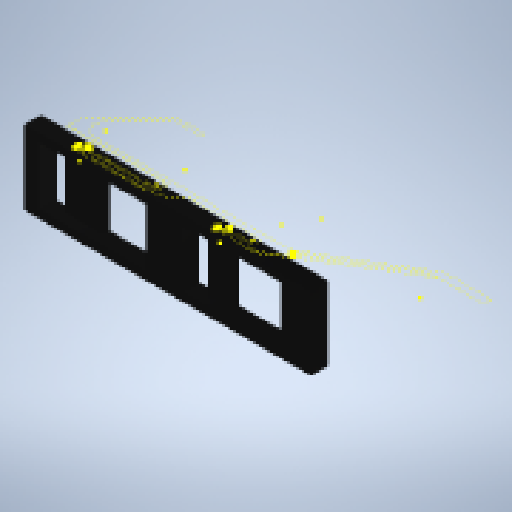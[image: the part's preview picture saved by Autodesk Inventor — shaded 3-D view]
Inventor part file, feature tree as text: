
AUTODESK INVENTOR PART (.ipt)
format: ipt  version: 2024.1 (Build 281209000, 209)  size: 655,360 bytes
history: native  units: mm
features: reference x29, projected_geometry x9, sketch x8, extrude x7, other x4, chamfer x4, plane x2, fillet x1
ambient origin geometry x8: Origin, YZ Plane, XZ Plane, XY Plane, X Axis, Y Axis, Z Axis, Center Point
bodies: Solid2 (feature_tree)
feature tree (64):
  other  "back-plate"
  plane  "Work Plane1"
  extrude  "Extrusion12"  Depth=19.0mm
  extrude  "Extrusion13"  Depth=47.0mm
  extrude  "Extrusion14"  Depth=19.2mm
  sketch  "Sketch14"  dims[d81=43.0mm]
  plane  "Work Plane2"
  chamfer  "Chamfer10"  Distance=1.5mm
  extrude  "Extrusion15"  Depth=15.0mm
  chamfer  "Chamfer11"  Distance=254.0mm
  extrude  "Extrusion5"  Depth=5.0mm TaperAngle=45.0deg
  sketch  "Sketch Driven Pattern1"  dims[d48=0.5mm d49=0.0mm d55=19.0mm d58=19.2mm]
  extrude  "Extrusion6"  Depth=15.0mm
  fillet  "Fillet2"  [1 undecoded]
  chamfer  "Chamfer7"  Distance=3.0mm Angle=45.0deg
  extrude  "Extrusion7"  Depth=10.0mm
  chamfer  "Chamfer8"  Distance=14.400658mm
  sketch  "Sketch7"  dims[d60=47.0mm d64=19.0mm]
  sketch  "Sketch8"  dims[d66=19.2mm d68=19.0mm d72=19.2mm d74=19.2mm d78=19.0mm d80=19.0mm]
  reference  "Reference23"
  reference  "Reference24"
  reference  "Reference25"
  reference  "Reference26"
  reference  "Reference27"
  reference  "Reference28"
  reference  "Reference29"
  reference  "Reference30"
  reference  "Reference31"
  reference  "Reference32"
  reference  "Reference33"
  reference  "Reference34"
  reference  "Reference35"
  reference  "Reference36"
  reference  "Reference37"
  reference  "Reference38"
  reference  "Reference39"
  reference  "Reference40"
  reference  "Reference41"
  sketch  "Sketch15"  dims[d82=43.0mm]
  reference  "Reference42"
  reference  "Reference43"
  reference  "Reference44"
  reference  "Reference46"
  reference  "Reference48"
  reference  "Reference52"
  reference  "Reference53"
  reference  "Reference56"
  reference  "Reference57"
  reference  "Reference59"
  sketch  "Sketch16"  dims[d83=43.0mm]
  sketch  "Sketch17"  dims[d84=43.0mm]
  projected_geometry  "Projected Loop12"
  sketch  "Sketch18"  dims[d88=43.0mm d90=1.5mm d91=0.0mm d92=15.0mm d97=254.0mm d98=5.0mm d99=2.0mm d100=45.0deg d101=3.1mm d112=0.0mm d113=0.0mm d114=3.0mm d115=2.0mm d116=45.0deg d134=10.0mm d143=14.400658mm d147=4.0mm d149=3.7mm d151=4.0mm d152=4.0mm d154=11.0mm d155=11.0mm d156=15.2mm d157=0.0mm d158=2.0mm d159=0.0mm d160=2.0mm d161=0.0mm d162=3.7mm d163=7.107566mm d164=1.0mm d165=2.0mm d166=45.0deg d167=4.0mm d168=2.0mm d169=15.2mm d170=0.0mm d171=2.0mm d172=2.0mm d173=45.0deg d174=4.0mm d175=0.5mm d176=4.199342mm d177=4.199342mm d178=0.1mm d179=0.1mm d180=19.2mm d181=74.892434mm d182=42.8mm d183=74.892434mm d184=74.892434mm d185=25.0mm d186=10.0mm d187=74.892434mm d188=74.892434mm d189=74.892434mm d190=19.2mm d193=116.0mm d194=0.5mm d195=5.607566mm d196=10.0mm d197=30.0mm d198=15.0mm d199=14.0mm d200=15.0mm d201=14.0mm d203=14.0mm d204=41.2mm d205=41.0mm d206=127.0mm d207=127.0mm]
  projected_geometry  "Projected Loop13"
  projected_geometry  "Projected Loop14"
  projected_geometry  "Projected Loop15"
  projected_geometry  "Projected Loop16"
  projected_geometry  "Projected Loop17"
  projected_geometry  "Projected Loop18"
  projected_geometry  "Projected Loop19"
  projected_geometry  "Projected Loop20"
  other  "<userpath>\Documents\0004-CAD\3D-cad-main\cable-hanger\VERSION3-largel-upright-hook.iam"
  other  "VERSION3-largel-upright-hook.iam"
  other  "cable-hanger-dual-large:1"
note: 1 required parameter value undecoded (feature->parameter linkage not recoverable at this tier; creation-order binding heuristic only, values carry confidence <= 0.55)
